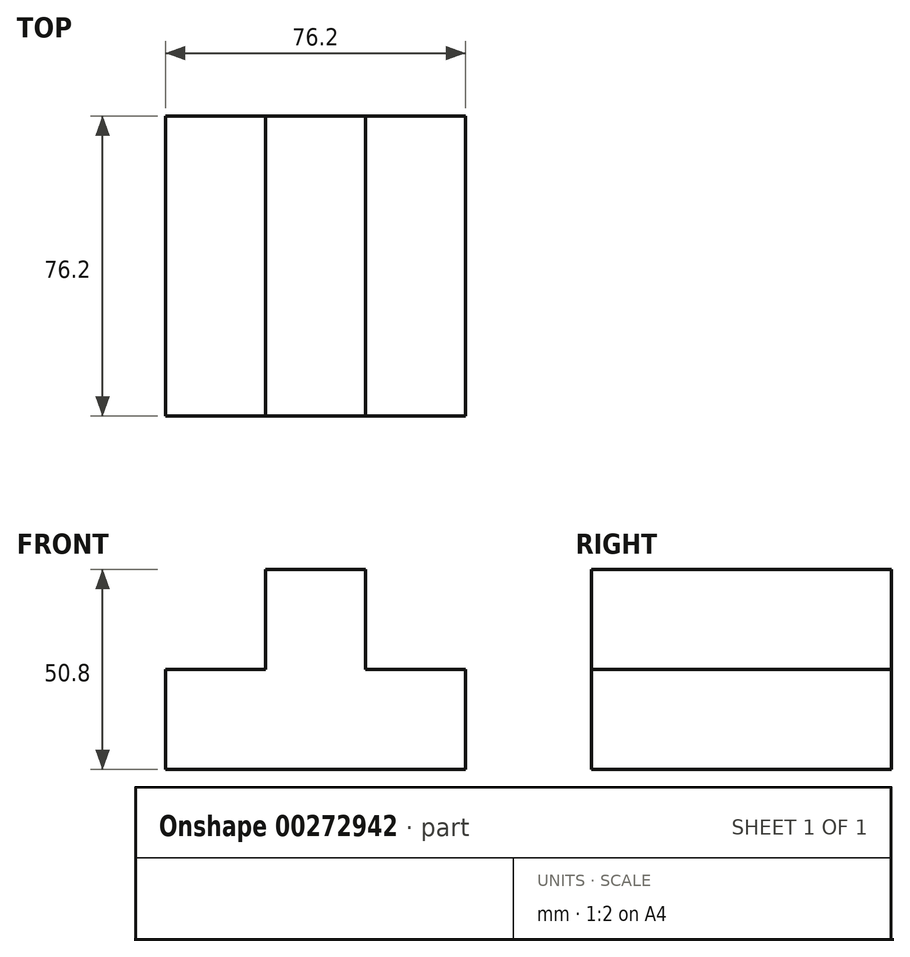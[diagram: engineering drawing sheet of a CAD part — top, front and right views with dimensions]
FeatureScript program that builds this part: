
annotation { "Feature Type Name" : "Feature", "Feature Type Description" : "" }
export const myFeature = defineFeature(function(context is Context, id is Id, definition is map)
    precondition{}
    {
        {
            var Q0;
            Q0=qCreatedBy(makeId("Front.planeOp"),FACE);
            var sketch = newSketch(context, id + "F0", { "sketchPlane" : qUnion([Q0])});
            skLineSegment(sketch, "E0", {"start": v(-39.15, 36.1) * mm, "end": v(-39.15, 10.7) * mm});
            skLineSegment(sketch, "E1", {"start": v(-39.15, 10.7) * mm, "end": v(37.05, 10.7) * mm});
            skLineSegment(sketch, "E2", {"start": v(37.05, 10.7) * mm, "end": v(37.05, 36.1) * mm});
            skLineSegment(sketch, "E3", {"start": v(37.05, 36.1) * mm, "end": v(11.65, 36.1) * mm});
            skLineSegment(sketch, "E4", {"start": v(11.65, 36.1) * mm, "end": v(11.65, 61.5) * mm});
            skLineSegment(sketch, "E5", {"start": v(11.65, 61.5) * mm, "end": v(-13.75, 61.5) * mm});
            skLineSegment(sketch, "E6", {"start": v(-13.75, 61.5) * mm, "end": v(-13.75, 36.1) * mm});
            skLineSegment(sketch, "E7", {"start": v(-13.75, 36.1) * mm, "end": v(-39.15, 36.1) * mm});
            skSolve(sketch);
        }
        {
            var Q0;
            Q0 = qSketchRegion(id + "F0", true);
            extrude(context, id + "F1", {"entities" : qUnion([Q0]), "depth" : 76.2 * mm});
        }
    });
